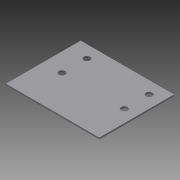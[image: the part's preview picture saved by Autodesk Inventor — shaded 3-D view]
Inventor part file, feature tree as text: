
AUTODESK INVENTOR PART (.ipt)
format: ipt  version: 2014 SP1 (Build 180222100, 222)  size: 91,136 bytes
history: native  units: in
note: dims shown in document units (in); Inventor stores cm internally (conversion verified against a paired STEP export)
features: sketch x2, extrude x1, hole x1
ambient origin geometry x8: Origin, YZ Plane, XZ Plane, XY Plane, X Axis, Y Axis, Z Axis, Center Point
bodies: Body1 (feature_tree)
feature tree (4):
  extrude  "Extrusion2"  Depth=3.0in
  hole  "Hole3"  [1 undecoded]
  sketch  "Sketch1"  dims[d0=3.75in d1=3.0in]
  sketch  "Sketch3"  dims[d14=0.5in d15=0.75in d16=2.5in d17=0.0625in d18=0.0in d19=0.75in d20=0.5in d21=2.5in d29=0.75in d30=1.5in d31=2.5in d32=1.0in d33=2.5in d34=0.75in d35=0.255in d36=0.75in d37=0.375in d38=0.25in d39=0.5635in d40=1.0in d41=0.8108in]
note: 1 required parameter value undecoded (feature->parameter linkage not recoverable at this tier; creation-order binding heuristic only, values carry confidence <= 0.55)
